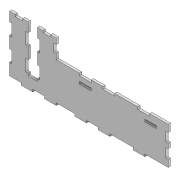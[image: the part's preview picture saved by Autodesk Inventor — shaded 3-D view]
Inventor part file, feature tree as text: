
AUTODESK INVENTOR PART (.ipt)
format: ipt  version: 2022 (Build 260153000, 153)  size: 360,960 bytes
history: native  units: mm
features: extrude x4, sketch x4, projected_geometry x3
ambient origin geometry x8: Origin, YZ Plane, XZ Plane, XY Plane, X Axis, Y Axis, Z Axis, Center Point
bodies: Solid1 (feature_tree)
feature tree (11):
  extrude  "Extrusion1"  Depth=40.0mm
  extrude  "Extrusion2"  Depth=25.0mm
  extrude  "Extrusion3"  Depth=25.0mm
  extrude  "Extrusion4"  Depth=5.0mm
  sketch  "Sketch1"  dims[d2=80.0mm d3=40.0mm]
  sketch  "Sketch2"  dims[d4=5.0mm d5=0.0mm d6=25.0mm]
  projected_geometry  "Projected Loop1"
  sketch  "Sketch3"  dims[d7=5.0mm d8=25.0mm]
  projected_geometry  "Projected Loop2"
  sketch  "Sketch4"  dims[d9=25.0mm d10=5.0mm d20=40.0mm d21=50.0mm d22=25.0mm d23=40.0mm d24=20.0mm d26=20.0mm d27=120.0mm d28=120.0mm d29=5.0mm d30=25.0mm d31=5.0mm d32=25.0mm d33=25.0mm d34=25.0mm d35=5.0mm d36=5.0mm d37=5.0mm d38=16.0mm d39=12.0mm d40=25.0mm d41=5.0mm d42=25.0mm d44=25.0mm d45=25.0mm d46=5.0mm d47=5.0mm d48=20.0mm d49=20.0mm d50=10.0mm d51=15.0mm d52=5.0mm d53=0.0mm d54=12.0mm d55=16.0mm d56=16.0mm d57=12.0mm d58=280.0mm d59=10.0mm d60=10.0mm d61=10.0mm d62=10.0mm d63=10.0mm d64=5.0mm d65=0.0mm d66=25.0mm d67=5.0mm d68=25.0mm d69=5.0mm d70=50.0mm d71=25.0mm d72=60.0mm d73=60.0mm d74=5.0mm d75=0.0mm]
  projected_geometry  "Projected Loop3"
